# Revit family: Geberit AquaClean 4000 akıllı klozet kapağı_PRO_100000
name_source: partatom
category: Plumbing Fixtures
revit_build: Autodesk Revit 2018 (Build: 20190510_1515(x64)
units: mm (PartAtom-declared; Revit-internal decimal feet)

## family parameters
Always vertical = Yes
Cut with Voids When Loaded = No
OmniClass Number = 23.45.05.21
OmniClass Title = Plumbing Fixtures - Sanitary Disposal Units
Part Type = Normal
Room Calculation Point = Yes
Round Connector Dimension = Use Diameter
Shared = No
Work Plane-Based = No

## types (1)
- 146.130.11.2 Geberit AquaClean 4000 akıllı klozet kapağı
    146030_0_view = Yes
    Application purposes = Konforlu klozet kullanımı için
Hassas bölgenin suyla tahriş etmeden temizlenmesi için
Klozet seramikleri üzerine sonradan montaj için (klozet oturağı için değişim)
    Application range = Plumbing fixture
    Article number key = 146.130.11.2
    BIM Content Version = GEB MG 1.2
    BIM Content revision date = 2020.05.18
    Brand = Geberit
    CW Connection = Yes
    Characteristics = Yavaş kapanan oturağı ve klozet kapağı
Entegre sıcak su boyleri
Taharet için uzatılabilir nozullu taharet mekanizması
Duş spreyi ayarı beş kademede ayarlanabilir
Temiz suyla taharet borusu için otomatik ön ve ilave temizleme
Duş spreyi, taharet işlemi sırasında yavaş ve sürekli soğur
Sıcak su boylerinin çalışma modu ayarlanabilir (AÇIK / KAPALI / Enerji tasarruf modu)
Sıcak su hazırlama için kullanıcı algılaması
Son kullanılan ayarlar otomatik olarak kaydedilir
Su bağlantısı sol yanda
Şebeke bağlantısı arkada, solda veya sağda gizli döşeme seçeneği ile
Elektrik kablosu kısaltılabilir
(DIN) EN 1717 / (DIN) EN 13077 uyarınca onaylı
    Description = Geberit AquaClean 4000 akıllı klozet kapağı
    EAN code basic data = 4025416228349
    GEB_culture = tr-TR
    GEB_generic_description = Bathroom collection
    GEB_generic_manufacturer = generic
    GEB_pimversion = 22.02.12
    GEB_processing_type = T
    GEB_reference = PRO_100000
    GEB_translations = {"ATT_10673":"EAN code basic data","ATT_10773":"Çalışma basıncı","ATT_10775":"Çalışma sıcaklığı","ATT_10786":"Hassas bölge tahareti akış hızı","ATT_10792":"Taharet süresi","ATT_10826":"Klozet oturağı için maksimum yük","ATT_10847":"Hesaplanan akış hızı için minimum akış basıncı","ATT_459792":"Renk / Yüzey","ATT_10851":"Nominal şebeke gerilimi","ATT_10853":"Şebeke frekansı","ATT_10817":"Güç tüketimi","applicationPurposes":"Application purposes","application_range":"Application range","brandName":"Brand","characteristics":"Characteristics","content_creator":"BIM Content creator","content_date_changed":"BIM Content revision date","content_version":"BIM Content Version","key 1000":"Article number key","name":"Name","productBrand":"Product brand","scopeOfDelivery":"Scope of delivery","type":"Type","ATT_10767":"Hesaplanan akış hızı","fixed_material":"Main material"}
    Güç tüketimi = 800 W
    HW Connection = No
    Hassas bölge tahareti akış hızı = 0.9-1.5 l/min
    Hesaplanan akış hızı = 0.0 L/s
    Hesaplanan akış hızı için minimum akış basıncı = 0.5 bar
    IfcDescription = Geberit AquaClean 4000 akıllı klozet kapağı
    IfcExportAs = IfcSanitaryTerminal
    IfcExportType = WCSEAT
    Klozet oturağı için maksimum yük = 150 kg
    LOD300 = No
    LOD400 = Yes
    Main material = Geberit, Plastic, Opaque white
    Manufacturer = Geberit
    Model = AquaClean 4000 (AquaClean 4000)
    Name = Geberit AquaClean 4000 akıllı klozet kapağı
    Nominal şebeke gerilimi = 230 V AC
    Product brand = AquaClean
    Renk / Yüzey = Beyaz
    Scope of delivery = Sol yan bağlantı için su bağlantı seti, sıva üstü rezervuar için
Sıçramaya karşı koruyucu
Klozet oturağı / klozet için dengeleme tamponu
Sabitleme malzemesi
    Taharet süresi = 20 s
    Type = AquaClean 4000 (AquaClean 4000)
    Vent Connection = No
    Waste Connection = Yes
    outlet_flow = 0.0 L/s
    Çalışma basıncı = 0.5-10 bar
    Çalışma sıcaklığı = 10–40 °C
    Şebeke frekansı = 50-60 Hz

## geometry (parser evidence)
native form markers: Blend x8, Sweep x13
no freeform markers — native parametric forms only
